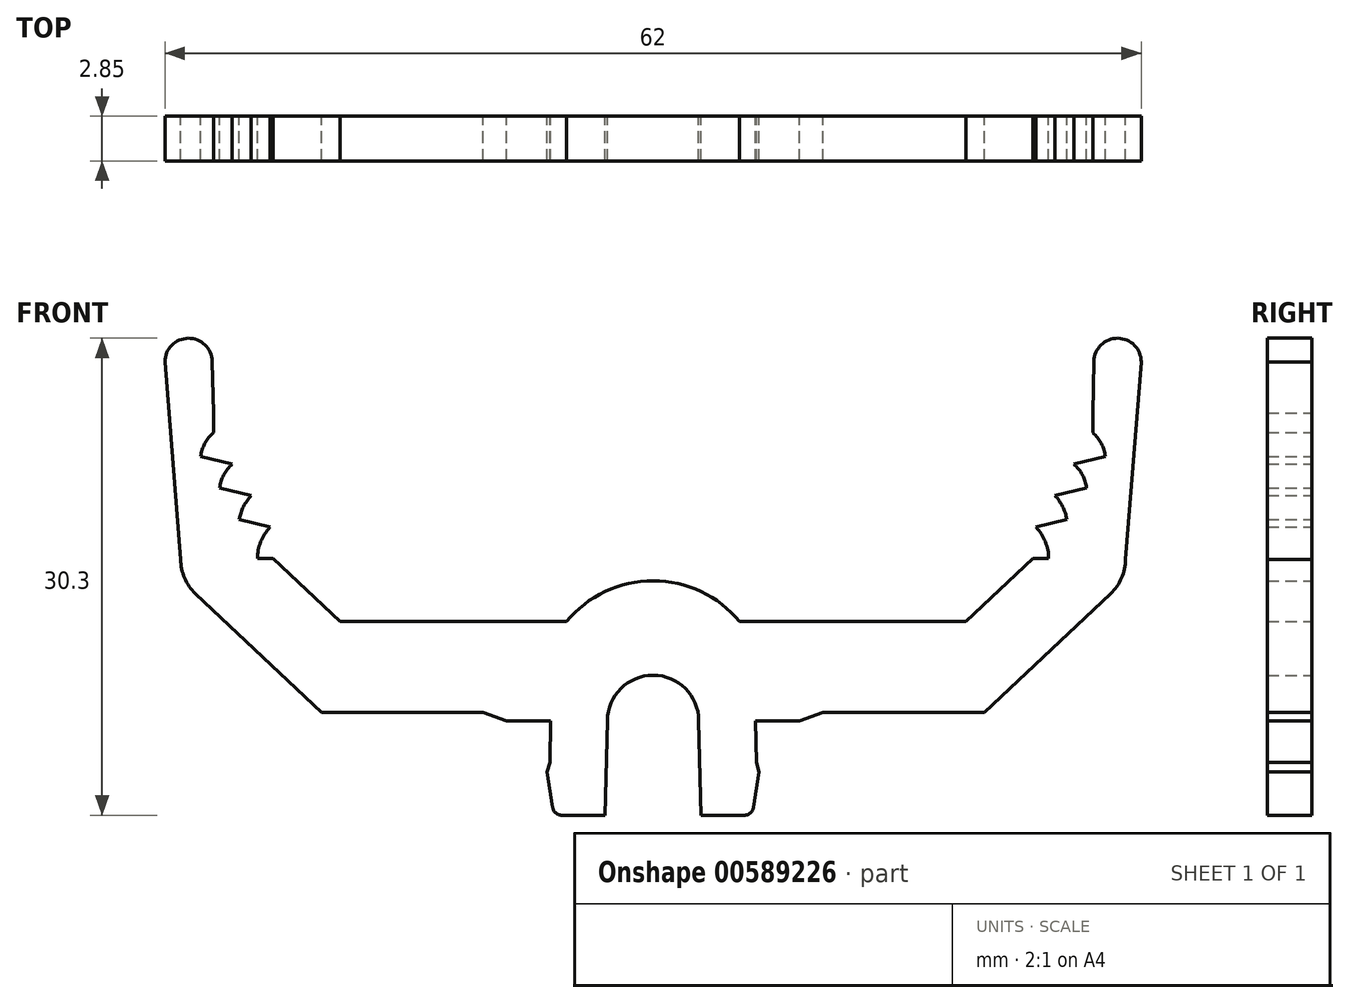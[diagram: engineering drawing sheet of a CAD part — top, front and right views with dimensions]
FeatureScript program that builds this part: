
annotation { "Feature Type Name" : "Feature", "Feature Type Description" : "" }
export const myFeature = defineFeature(function(context is Context, id is Id, definition is map)
    precondition{}
    {
        {
            var Q0;
            Q0=qCreatedBy(makeId("Front.planeOp"),FACE);
            var sketch = newSketch(context, id + "F0", { "sketchPlane" : qUnion([Q0])});
            skLineSegment(sketch, "E0.bottom", {"start": v(-19.87, 25.82) * mm, "end": v(-5.5, 25.82) * mm});
            skPoint(sketch, "E0.middle", {"position": v(0, 22.94) * mm});
            skLineSegment(sketch, "E1.bottom", {"start": v(-9.3, 19.52) * mm, "end": v(-6.5, 19.52) * mm});
            skPoint(sketch, "E1.middle", {"position": v(0, 20.07) * mm});
            skLineSegment(sketch, "E2", {"start": v(-9.3, 19.52) * mm, "end": v(-10.8, 20.07) * mm});
            skLineSegment(sketch, "E3.MirrorCS", {"start": v(9.3, 19.52) * mm, "end": v(10.8, 20.07) * mm});
            skPoint(sketch, "E4.orphan", {"position": v(-9.3, 20.62) * mm});
            skPoint(sketch, "E1.right.end.orphan", {"position": v(9.3, 20.62) * mm});
            skLineSegment(sketch, "E5.trimOffspring", {"start": v(5.5, 25.82) * mm, "end": v(19.87, 25.82) * mm});
            skLineSegment(sketch, "E6", {"start": v(19.88, 25.82) * mm, "end": v(24.13, 29.82) * mm});
            skLineSegment(sketch, "E7", {"start": v(24.12, 29.82) * mm, "end": v(25.12, 29.82) * mm});
            skArc(sketch, "E8", {"start": v(25.13, 29.82) * mm, "mid": v(24.92, 30.9) * mm, "end": v(24.33, 31.82) * mm});
            skLineSegment(sketch, "E9", {"start": v(25.12, 29.82) * mm, "end": v(25.12, 31.12) * mm, "construction": true});
            skLineSegment(sketch, "E10", {"start": v(24.32, 31.82) * mm, "end": v(26.33, 31.82) * mm, "construction": true});
            skArc(sketch, "E11", {"start": v(26.33, 31.82) * mm, "mid": v(26.12, 32.9) * mm, "end": v(25.53, 33.82) * mm});
            skLineSegment(sketch, "E12", {"start": v(26.33, 31.82) * mm, "end": v(26.33, 33.04) * mm, "construction": true});
            skLineSegment(sketch, "E13", {"start": v(25.53, 33.82) * mm, "end": v(27.53, 33.82) * mm, "construction": true});
            skArc(sketch, "E14", {"start": v(27.53, 33.82) * mm, "mid": v(27.37, 34.92) * mm, "end": v(26.73, 35.82) * mm});
            skLineSegment(sketch, "E15", {"start": v(26.73, 35.82) * mm, "end": v(28.73, 35.82) * mm, "construction": true});
            skArc(sketch, "E16", {"start": v(28.73, 35.82) * mm, "mid": v(28.57, 36.92) * mm, "end": v(27.93, 37.82) * mm});
            skLineSegment(sketch, "E17", {"start": v(27.93, 37.82) * mm, "end": v(27.93, 39.07) * mm});
            skLineSegment(sketch, "E18.0", {"start": v(21.06, 20.07) * mm, "end": v(29.06, 27.6) * mm});
            skPoint(sketch, "E19.visualSharp", {"position": v(31.73, 30.1) * mm});
            skArc(sketch, "E19.filletArc", {"start": v(29.06, 27.6) * mm, "mid": v(29.75, 28.59) * mm, "end": v(30, 29.78) * mm});
            skArc(sketch, "E20", {"start": v(31, 42.32) * mm, "mid": v(29.52, 43.82) * mm, "end": v(28, 42.35) * mm});
            skPoint(sketch, "E21", {"position": v(29.5, 43.82) * mm});
            skLineSegment(sketch, "E22", {"start": v(27.93, 39.07) * mm, "end": v(28, 42.35) * mm});
            skPoint(sketch, "E23.orphan", {"position": v(31.6, 43.82) * mm});
            skLineSegment(sketch, "E24.MirrorCS", {"start": v(-25.12, 29.82) * mm, "end": v(-25.12, 31.12) * mm, "construction": true});
            skLineSegment(sketch, "E25.MirrorCS", {"start": v(-24.32, 31.82) * mm, "end": v(-26.33, 31.82) * mm, "construction": true});
            skArc(sketch, "E26.MirrorCS", {"start": v(-26.33, 31.82) * mm, "mid": v(-26.12, 32.9) * mm, "end": v(-25.53, 33.82) * mm});
            skLineSegment(sketch, "E27.MirrorCS", {"start": v(-24.12, 29.82) * mm, "end": v(-25.12, 29.82) * mm});
            skArc(sketch, "E28.MirrorCS", {"start": v(-27.53, 33.82) * mm, "mid": v(-27.37, 34.92) * mm, "end": v(-26.73, 35.82) * mm});
            skArc(sketch, "E29.MirrorCS", {"start": v(-25.13, 29.82) * mm, "mid": v(-24.92, 30.9) * mm, "end": v(-24.33, 31.82) * mm});
            skLineSegment(sketch, "E30.MirrorCS", {"start": v(-26.33, 31.82) * mm, "end": v(-26.33, 33.04) * mm, "construction": true});
            skLineSegment(sketch, "E31.MirrorCS", {"start": v(-27.93, 37.82) * mm, "end": v(-27.93, 39.07) * mm});
            skLineSegment(sketch, "E32.MirrorCS", {"start": v(-27.93, 39.07) * mm, "end": v(-28, 42.35) * mm});
            skArc(sketch, "E33.MirrorCS", {"start": v(-28.73, 35.82) * mm, "mid": v(-28.57, 36.92) * mm, "end": v(-27.93, 37.82) * mm});
            skLineSegment(sketch, "E34.MirrorCS", {"start": v(-26.73, 35.82) * mm, "end": v(-28.73, 35.82) * mm, "construction": true});
            skLineSegment(sketch, "E35.MirrorCS", {"start": v(-25.53, 33.82) * mm, "end": v(-27.53, 33.82) * mm, "construction": true});
            skArc(sketch, "E36.MirrorCS", {"start": v(-29.06, 27.6) * mm, "mid": v(-29.75, 28.59) * mm, "end": v(-30, 29.78) * mm});
            skArc(sketch, "E37.MirrorCS", {"start": v(-31, 42.32) * mm, "mid": v(-29.52, 43.82) * mm, "end": v(-28, 42.35) * mm});
            skLineSegment(sketch, "E38.MirrorCS", {"start": v(-19.88, 25.82) * mm, "end": v(-24.13, 29.82) * mm});
            skLineSegment(sketch, "E39.MirrorCS", {"start": v(-21.06, 20.07) * mm, "end": v(-29.06, 27.6) * mm});
            skPoint(sketch, "E40.MirrorP", {"position": v(-31.6, 43.82) * mm});
            skPoint(sketch, "E41.MirrorP", {"position": v(-31.73, 30.1) * mm});
            skPoint(sketch, "E42.MirrorP", {"position": v(-29.5, 43.82) * mm});
            skLineSegment(sketch, "E43", {"start": v(-2.9, 19.52) * mm, "end": v(-3.04, 13.52) * mm});
            skLineSegment(sketch, "E44", {"start": v(-6.5, 19.52) * mm, "end": v(-6.56, 16.87) * mm});
            skLineSegment(sketch, "E45", {"start": v(-6.56, 16.87) * mm, "end": v(-6.73, 16.27) * mm});
            skLineSegment(sketch, "E46", {"start": v(-6.73, 16.27) * mm, "end": v(-6.38, 14.03) * mm});
            skLineSegment(sketch, "E47", {"start": v(-5.79, 13.52) * mm, "end": v(-3.04, 13.52) * mm});
            skLineSegment(sketch, "E48.MirrorCS", {"start": v(5.79, 13.52) * mm, "end": v(3.04, 13.52) * mm});
            skLineSegment(sketch, "E49.MirrorCS", {"start": v(6.56, 16.87) * mm, "end": v(6.73, 16.27) * mm});
            skLineSegment(sketch, "E50.MirrorCS", {"start": v(2.9, 19.52) * mm, "end": v(3.04, 13.52) * mm});
            skLineSegment(sketch, "E51.MirrorCS", {"start": v(6.73, 16.27) * mm, "end": v(6.38, 14.03) * mm});
            skLineSegment(sketch, "E52.MirrorCS", {"start": v(6.5, 19.52) * mm, "end": v(6.56, 16.87) * mm});
            skArc(sketch, "E53", {"start": v(-2.9, 19.52) * mm, "mid": v(0, 22.42) * mm, "end": v(2.9, 19.52) * mm});
            skPoint(sketch, "E54.visualSharp", {"position": v(-6.3, 13.52) * mm});
            skArc(sketch, "E54.filletArc", {"start": v(-6.38, 14.03) * mm, "mid": v(-6.18, 13.66) * mm, "end": v(-5.79, 13.52) * mm});
            skPoint(sketch, "E55.visualSharp", {"position": v(6.3, 13.52) * mm});
            skArc(sketch, "E55.filletArc", {"start": v(5.79, 13.52) * mm, "mid": v(6.18, 13.66) * mm, "end": v(6.38, 14.03) * mm});
            skLineSegment(sketch, "E56.trimOffspring", {"start": v(6.5, 19.52) * mm, "end": v(9.3, 19.52) * mm});
            skLineSegment(sketch, "E57", {"start": v(10.8, 20.07) * mm, "end": v(21.06, 20.07) * mm});
            skLineSegment(sketch, "E58", {"start": v(-21.06, 20.07) * mm, "end": v(-10.8, 20.07) * mm});
            skLineSegment(sketch, "E59", {"start": v(-31, 42.32) * mm, "end": v(-30, 29.78) * mm});
            skLineSegment(sketch, "E60", {"start": v(31, 42.32) * mm, "end": v(30, 29.78) * mm});
            skArc(sketch, "E61", {"start": v(5.5, 25.82) * mm, "mid": v(0, 28.42) * mm, "end": v(-5.5, 25.82) * mm});
            skLineSegment(sketch, "E62", {"start": v(24.32, 31.82) * mm, "end": v(26.28, 32.32) * mm});
            skLineSegment(sketch, "E63", {"start": v(25.53, 33.82) * mm, "end": v(27.52, 34.32) * mm});
            skLineSegment(sketch, "E64", {"start": v(26.72, 35.82) * mm, "end": v(28.72, 36.32) * mm});
            skLineSegment(sketch, "E65.MirrorCS", {"start": v(-26.72, 35.82) * mm, "end": v(-28.72, 36.32) * mm});
            skLineSegment(sketch, "E66.MirrorCS", {"start": v(-25.52, 33.82) * mm, "end": v(-27.52, 34.32) * mm});
            skLineSegment(sketch, "E67.MirrorCS", {"start": v(-24.32, 31.82) * mm, "end": v(-26.28, 32.32) * mm});
            skLineSegment(sketch, "E68", {"start": v(-30, 29.82) * mm, "end": v(30, 29.82) * mm, "construction": true});
            skSolve(sketch);
        }
        {
            var Q0;
            Q0=makeQuery(id+"F0.imprint","IMPRINT",FACE,{"disambiguationData":[TD([[makeQuery(id+"F0.imprint","IMPRINT",EDGE,{"derivedFrom":sQuery(id+"F0.wireOp",EDGE,"E0.bottom")}),-1.0]])]});
            extrude(context, id + "F1", {"entities" : qUnion([Q0]), "depth" : 2.85 * mm, "offsetDistance" : 25 * mm});
        }
    });
